# Revit family: 5972 Вазон «Олеандр» Хоббика
name_source: partatom
category: Антураж
revit_build: Autodesk Revit 2018 (Build: 20180423_1000(x64)
units: mm (PartAtom-declared; Revit-internal decimal feet)

## family parameters
Всегда вертикально = Да
Источник визуального образа = Геометрия семейства
На основе рабочей плоскости = Нет
Общий = Нет
При загрузке вырезать с полостями = Нет
Точка расчета площади = Нет

## types (3) — shared parameters
URL = https://hobbyka.ru
Артикул товара = Арт. 59972
Группа модели = Цветочницы и уличные вазоны для цветов
Изготовитель = ООО «Хоббика»
Изображение типоразмера = Вазон «Олеандр» Арт 59972.jpg
Материал изделия = Сталь, Дерево
Цвет каркаса = Сталь
Цвет отделки = Дерево

## per-type parameters (varying)
| type | Версия 1000х1000 | Версия 1300х1300 | Версия 700х700 | Высота | Длина | Описание | Ширина |
| Версия 700х700 | Нет | Нет | Да | 730 мм | 700 мм | Вазон «Олеандр». Версия 700х700 мм | 700 мм |
| Версия 1000х1000 | Да | Нет | Нет | 1000 мм | 1000 мм | Вазон «Олеандр». Версия 1000х1000 мм | 1000 мм |
| Версия 1300х1300 | Нет | Да | Нет | 1300 мм | 1300 мм | Вазон «Олеандр». Версия 1300х1300 мм | 1300 мм |
